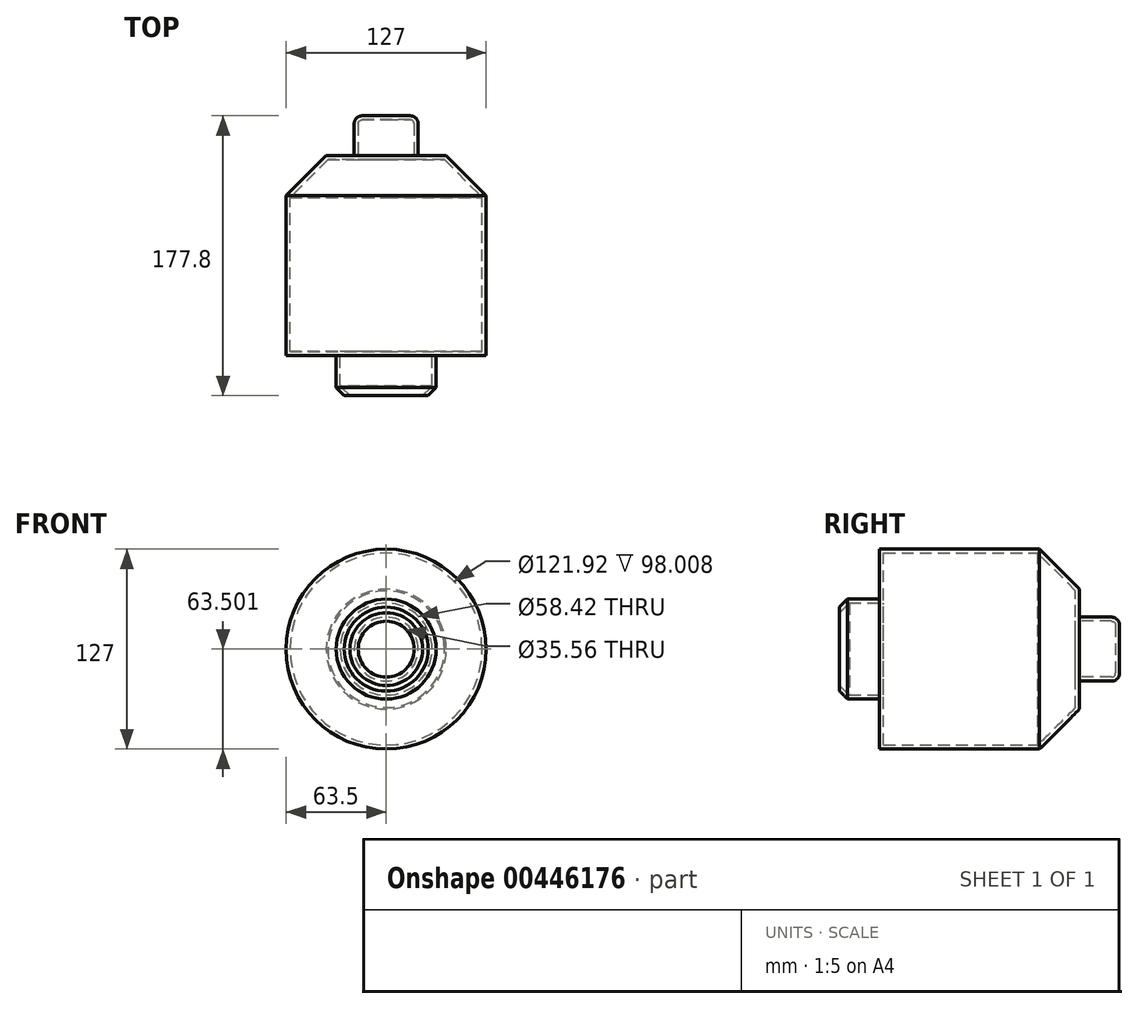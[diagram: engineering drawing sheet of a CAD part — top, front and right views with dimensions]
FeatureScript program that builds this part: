
annotation { "Feature Type Name" : "Feature", "Feature Type Description" : "" }
export const myFeature = defineFeature(function(context is Context, id is Id, definition is map)
    precondition{}
    {
        {
            var Q0;
            Q0=qCreatedBy(makeId("Front.planeOp"),FACE);
            var sketch = newSketch(context, id + "F0", { "sketchPlane" : qUnion([Q0])});
            skCircle(sketch, "E0", {"center": v(0, 42.2) * mm, "radius": 63.5 * mm});
            skPoint(sketch, "E1", {"position": v(0, 0) * mm});
            skSolve(sketch);
        }
        {
            var Q0;
            Q0 = qSketchRegion(id + "F0", true);
            extrude(context, id + "F1", {"entities" : qUnion([Q0]), "depth" : 127 * mm});
        }
        {
            var Q0;
            Q0=makeQuery(id+"F1.opExtrude","CAP_FACE",FACE,{"disambiguationData":[OSD([sQuery(id+"F0.wireOp",EDGE,"E0")])],"isStart":false});
            var sketch = newSketch(context, id + "F2", { "sketchPlane" : qUnion([Q0])});
            skCircle(sketch, "E2", {"center": v(0, 42.2) * mm, "radius": 31.75 * mm});
            skSolve(sketch);
        }
        {
            var Q0;
            Q0 = qSketchRegion(id + "F2", true);
            extrude(context, id + "F3", {"entities" : qUnion([Q0]), "operationType" : NewBodyOperationType.ADD, "depth" : 25.4 * mm});
        }
        {
            var Q0;
            Q0=makeQuery(id+"F1.opExtrude","CAP_FACE",FACE,{"disambiguationData":[OSD([sQuery(id+"F0.wireOp",EDGE,"E0")])],"isStart":true});
            var sketch = newSketch(context, id + "F4", { "sketchPlane" : qUnion([Q0])});
            skCircle(sketch, "E3", {"center": v(0, 42.2) * mm, "radius": 20.32 * mm});
            skSolve(sketch);
        }
        {
            var Q0;
            Q0 = qSketchRegion(id + "F4", true);
            extrude(context, id + "F5", {"entities" : qUnion([Q0]), "operationType" : NewBodyOperationType.ADD, "depth" : 25.4 * mm});
        }
        {
            var Q0;
            Q0=makeQuery(id+"F5.opExtrude","CAP_EDGE",EDGE,{"disambiguationData":[OSD([sQuery(id+"F4.wireOp",EDGE,"E3")])],"isStart":false});
            fillet(context, id + "F6", {"entities" : qUnion([Q0]), "radius" : 5.08 * mm, "tangentPropagation" : true, "allowEdgeOverflow" : false});
        }
        {
            var Q0;
            Q0=makeQuery(id+"F1.opExtrude","CAP_EDGE",EDGE,{"disambiguationData":[OSD([sQuery(id+"F0.wireOp",EDGE,"E0")])],"isStart":true});
            chamfer(context, id + "F7", {"entities" : qUnion([Q0]), "width" : 25.4 * mm, "tangentPropagation" : true});
        }
        {
            var Q0;
            Q0=makeQuery(id+"F3.opExtrude","CAP_EDGE",EDGE,{"disambiguationData":[OSD([sQuery(id+"F2.wireOp",EDGE,"E2")])],"isStart":false});
            chamfer(context, id + "F8", {"entities" : qUnion([Q0]), "width" : 5.08 * mm, "tangentPropagation" : true});
        }
        {
            var Q0;
            Q0=makeQuery(id+"F3.opExtrude","CAP_FACE",FACE,{"disambiguationData":[OSD([sQuery(id+"F2.wireOp",EDGE,"E2")])],"isStart":false});
            shell(context, id + "F9", {"entities" : qUnion([Q0]), "thickness" : 2.54 * mm});
        }
    });
